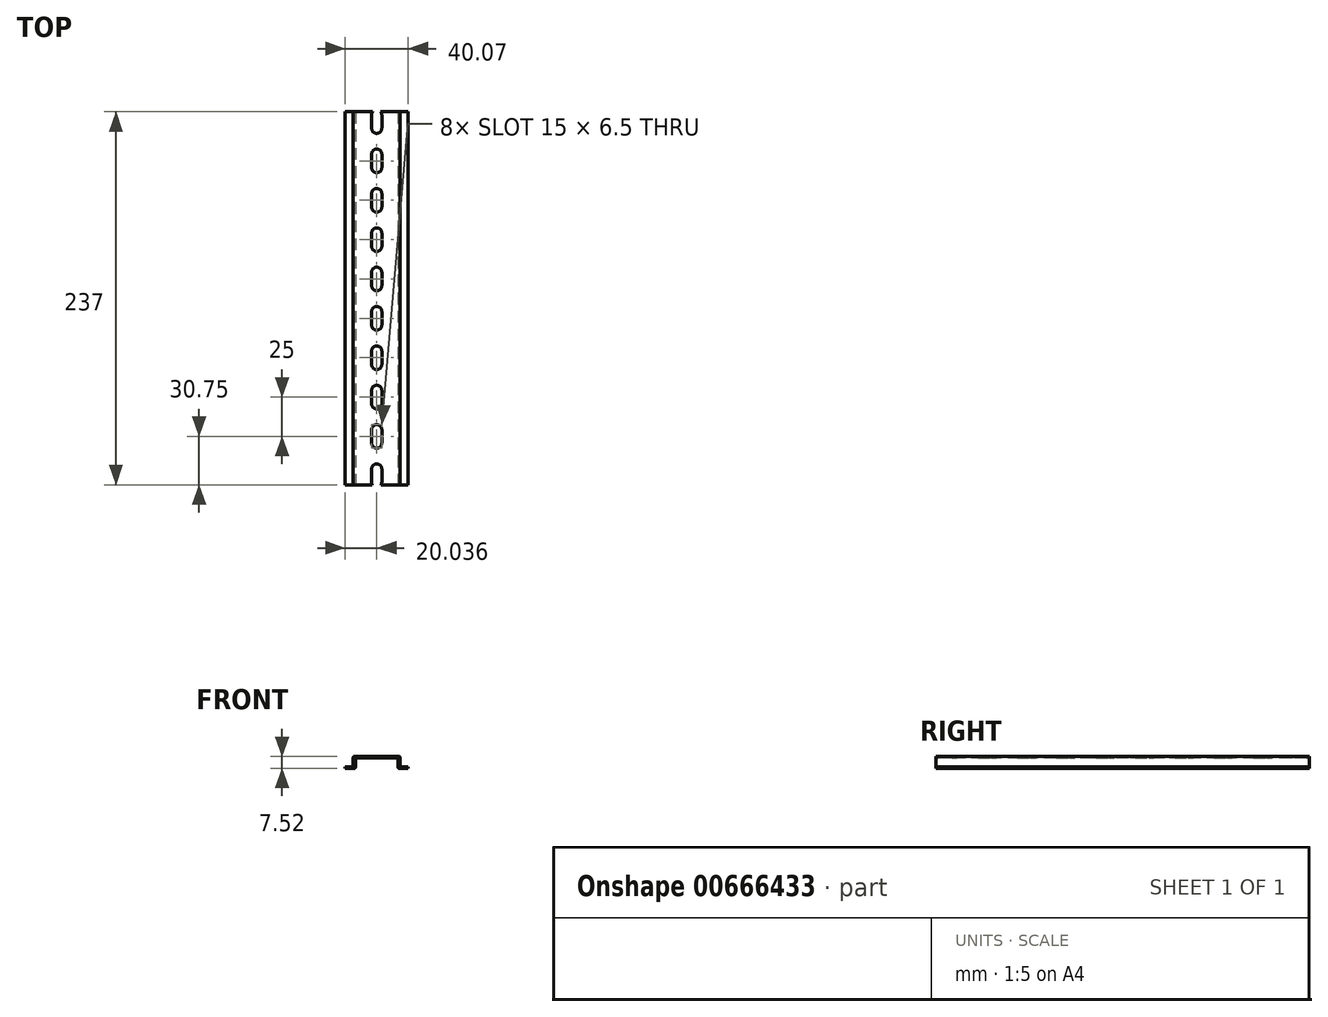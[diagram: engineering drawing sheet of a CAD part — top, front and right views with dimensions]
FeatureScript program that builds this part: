
annotation { "Feature Type Name" : "Feature", "Feature Type Description" : "" }
export const myFeature = defineFeature(function(context is Context, id is Id, definition is map)
    precondition{}
    {
        {
            var Q0;
            Q0=qCreatedBy(makeId("Front.planeOp"),FACE);
            var sketch = newSketch(context, id + "F0", { "sketchPlane" : qUnion([Q0])});
            skLineSegment(sketch, "E0.0", {"start": v(0, 1.23) * mm, "end": v(5.15, 1.49) * mm});
            skLineSegment(sketch, "E1.0.1", {"start": v(40.07, 1.23) * mm, "end": v(34.92, 1.49) * mm});
            skLineSegment(sketch, "E1.0.2", {"start": v(34.92, 1.49) * mm, "end": v(34.92, 7.31) * mm});
            skArc(sketch, "E1.0.3", {"start": v(34.92, 7.31) * mm, "mid": v(34.71, 7.8) * mm, "end": v(34.22, 8.01) * mm});
            skLineSegment(sketch, "E1.0.4", {"start": v(34.22, 8.01) * mm, "end": v(5.85, 8.01) * mm});
            skArc(sketch, "E1.0.5", {"start": v(5.85, 8.01) * mm, "mid": v(5.36, 7.8) * mm, "end": v(5.15, 7.31) * mm});
            skLineSegment(sketch, "E1.0.6", {"start": v(5.15, 7.31) * mm, "end": v(5.15, 1.49) * mm});
            skLineSegment(sketch, "E1.0.7", {"start": v(5.15, 1.49) * mm, "end": v(0, 1.23) * mm});
            skLineSegment(sketch, "E1.0.9", {"start": v(0, 0.49) * mm, "end": v(5.95, 0.49) * mm});
            skArc(sketch, "E1.0.10", {"start": v(5.95, 0.49) * mm, "mid": v(6.3, 0.63) * mm, "end": v(6.45, 0.99) * mm});
            skLineSegment(sketch, "E1.0.11", {"start": v(6.45, 0.99) * mm, "end": v(6.45, 6.71) * mm});
            skArc(sketch, "E1.0.12", {"start": v(6.45, 6.71) * mm, "mid": v(6.54, 6.93) * mm, "end": v(6.75, 7.01) * mm});
            skLineSegment(sketch, "E1.0.13", {"start": v(6.75, 7.01) * mm, "end": v(33.32, 7.01) * mm});
            skArc(sketch, "E1.0.14", {"start": v(33.32, 7.01) * mm, "mid": v(33.53, 6.93) * mm, "end": v(33.62, 6.71) * mm});
            skLineSegment(sketch, "E1.0.15", {"start": v(33.62, 6.71) * mm, "end": v(33.62, 0.99) * mm});
            skArc(sketch, "E1.0.16", {"start": v(33.62, 0.99) * mm, "mid": v(33.77, 0.63) * mm, "end": v(34.12, 0.49) * mm});
            skLineSegment(sketch, "E1.0.17", {"start": v(34.12, 0.49) * mm, "end": v(40.07, 0.49) * mm});
            skLineSegment(sketch, "E2", {"start": v(0, 1.23) * mm, "end": v(0, 0.49) * mm});
            skLineSegment(sketch, "E3", {"start": v(40.07, 1.23) * mm, "end": v(40.07, 0.49) * mm});
            skSolve(sketch);
        }
        {
            var Q0;
            Q0=qSketchRegion(id+"F0",true);
            extrude(context, id + "F1", {"entities" : qUnion([Q0]), "oppositeDirection" : true, "depth" : 237 * mm, "offsetDistance" : 25 * mm});
        }
        {
            var Q0;
            Q0=qCreatedBy(makeId("Top.planeOp"),FACE);
            var sketch = newSketch(context, id + "F2", { "sketchPlane" : qUnion([Q0])});
            skLineSegment(sketch, "E4.0", {"start": v(16.79, 10) * mm, "end": v(16.79, 1.5) * mm});
            skArc(sketch, "E5.0", {"start": v(23.29, 10) * mm, "mid": v(20.04, 13.25) * mm, "end": v(16.79, 10) * mm});
            skLineSegment(sketch, "E6.0", {"start": v(23.29, 1.5) * mm, "end": v(23.29, 10) * mm});
            skArc(sketch, "E7.0", {"start": v(16.79, 1.5) * mm, "mid": v(20.04, -1.75) * mm, "end": v(23.29, 1.5) * mm});
            skArc(sketch, "E8.0.1.0", {"start": v(16.79, 26.5) * mm, "mid": v(20.04, 23.25) * mm, "end": v(23.29, 26.5) * mm});
            skArc(sketch, "E8.0.1.1", {"start": v(23.29, 35) * mm, "mid": v(20.04, 38.25) * mm, "end": v(16.79, 35) * mm});
            skLineSegment(sketch, "E8.0.1.2", {"start": v(16.79, 35) * mm, "end": v(16.79, 26.5) * mm});
            skLineSegment(sketch, "E8.0.1.3", {"start": v(23.29, 26.5) * mm, "end": v(23.29, 35) * mm});
            skArc(sketch, "E8.0.2.0", {"start": v(16.79, 51.5) * mm, "mid": v(20.04, 48.25) * mm, "end": v(23.29, 51.5) * mm});
            skArc(sketch, "E8.0.2.1", {"start": v(23.29, 60) * mm, "mid": v(20.04, 63.25) * mm, "end": v(16.79, 60) * mm});
            skLineSegment(sketch, "E8.0.2.2", {"start": v(16.79, 60) * mm, "end": v(16.79, 51.5) * mm});
            skLineSegment(sketch, "E8.0.2.3", {"start": v(23.29, 51.5) * mm, "end": v(23.29, 60) * mm});
            skArc(sketch, "E8.0.3.0", {"start": v(16.79, 76.5) * mm, "mid": v(20.04, 73.25) * mm, "end": v(23.29, 76.5) * mm});
            skArc(sketch, "E8.0.3.1", {"start": v(23.29, 85) * mm, "mid": v(20.04, 88.25) * mm, "end": v(16.79, 85) * mm});
            skLineSegment(sketch, "E8.0.3.2", {"start": v(16.79, 85) * mm, "end": v(16.79, 76.5) * mm});
            skLineSegment(sketch, "E8.0.3.3", {"start": v(23.29, 76.5) * mm, "end": v(23.29, 85) * mm});
            skArc(sketch, "E8.0.4.0", {"start": v(16.79, 101.5) * mm, "mid": v(20.04, 98.25) * mm, "end": v(23.29, 101.5) * mm});
            skArc(sketch, "E8.0.4.1", {"start": v(23.29, 110) * mm, "mid": v(20.04, 113.25) * mm, "end": v(16.79, 110) * mm});
            skLineSegment(sketch, "E8.0.4.2", {"start": v(16.79, 110) * mm, "end": v(16.79, 101.5) * mm});
            skLineSegment(sketch, "E8.0.4.3", {"start": v(23.29, 101.5) * mm, "end": v(23.29, 110) * mm});
            skArc(sketch, "E8.0.5.0", {"start": v(16.79, 126.5) * mm, "mid": v(20.04, 123.25) * mm, "end": v(23.29, 126.5) * mm});
            skArc(sketch, "E8.0.5.1", {"start": v(23.29, 135) * mm, "mid": v(20.04, 138.25) * mm, "end": v(16.79, 135) * mm});
            skLineSegment(sketch, "E8.0.5.2", {"start": v(16.79, 135) * mm, "end": v(16.79, 126.5) * mm});
            skLineSegment(sketch, "E8.0.5.3", {"start": v(23.29, 126.5) * mm, "end": v(23.29, 135) * mm});
            skArc(sketch, "E8.0.6.0", {"start": v(16.79, 151.5) * mm, "mid": v(20.04, 148.25) * mm, "end": v(23.29, 151.5) * mm});
            skArc(sketch, "E8.0.6.1", {"start": v(23.29, 160) * mm, "mid": v(20.04, 163.25) * mm, "end": v(16.79, 160) * mm});
            skLineSegment(sketch, "E8.0.6.2", {"start": v(16.79, 160) * mm, "end": v(16.79, 151.5) * mm});
            skLineSegment(sketch, "E8.0.6.3", {"start": v(23.29, 151.5) * mm, "end": v(23.29, 160) * mm});
            skArc(sketch, "E8.0.7.0", {"start": v(16.79, 176.5) * mm, "mid": v(20.04, 173.25) * mm, "end": v(23.29, 176.5) * mm});
            skArc(sketch, "E8.0.7.1", {"start": v(23.29, 185) * mm, "mid": v(20.04, 188.25) * mm, "end": v(16.79, 185) * mm});
            skLineSegment(sketch, "E8.0.7.2", {"start": v(16.79, 185) * mm, "end": v(16.79, 176.5) * mm});
            skLineSegment(sketch, "E8.0.7.3", {"start": v(23.29, 176.5) * mm, "end": v(23.29, 185) * mm});
            skArc(sketch, "E8.0.8.0", {"start": v(16.79, 201.5) * mm, "mid": v(20.04, 198.25) * mm, "end": v(23.29, 201.5) * mm});
            skArc(sketch, "E8.0.8.1", {"start": v(23.29, 210) * mm, "mid": v(20.04, 213.25) * mm, "end": v(16.79, 210) * mm});
            skLineSegment(sketch, "E8.0.8.2", {"start": v(16.79, 210) * mm, "end": v(16.79, 201.5) * mm});
            skLineSegment(sketch, "E8.0.8.3", {"start": v(23.29, 201.5) * mm, "end": v(23.29, 210) * mm});
            skArc(sketch, "E8.0.9.0", {"start": v(16.79, 226.5) * mm, "mid": v(20.04, 223.25) * mm, "end": v(23.29, 226.5) * mm});
            skArc(sketch, "E8.0.9.1", {"start": v(23.29, 235) * mm, "mid": v(20.04, 238.25) * mm, "end": v(16.79, 235) * mm});
            skLineSegment(sketch, "E8.0.9.2", {"start": v(16.79, 235) * mm, "end": v(16.79, 226.5) * mm});
            skLineSegment(sketch, "E8.0.9.3", {"start": v(23.29, 226.5) * mm, "end": v(23.29, 235) * mm});
            skLineSegment(sketch, "E8.direction1", {"start": v(16.79, 1.5) * mm, "end": v(41.79, 1.5) * mm, "construction": true});
            skLineSegment(sketch, "E8.direction2", {"start": v(16.79, 1.5) * mm, "end": v(16.79, 26.5) * mm, "construction": true});
            skSolve(sketch);
        }
        {
            var Q0;
            Q0=qSketchRegion(id+"F2",true);
            extrude(context, id + "F3", {"entities" : qUnion([Q0]), "operationType" : NewBodyOperationType.REMOVE, "endBound" : BoundingType.THROUGH_ALL, "depth" : 25 * mm, "offsetDistance" : 25 * mm});
        }
    });
